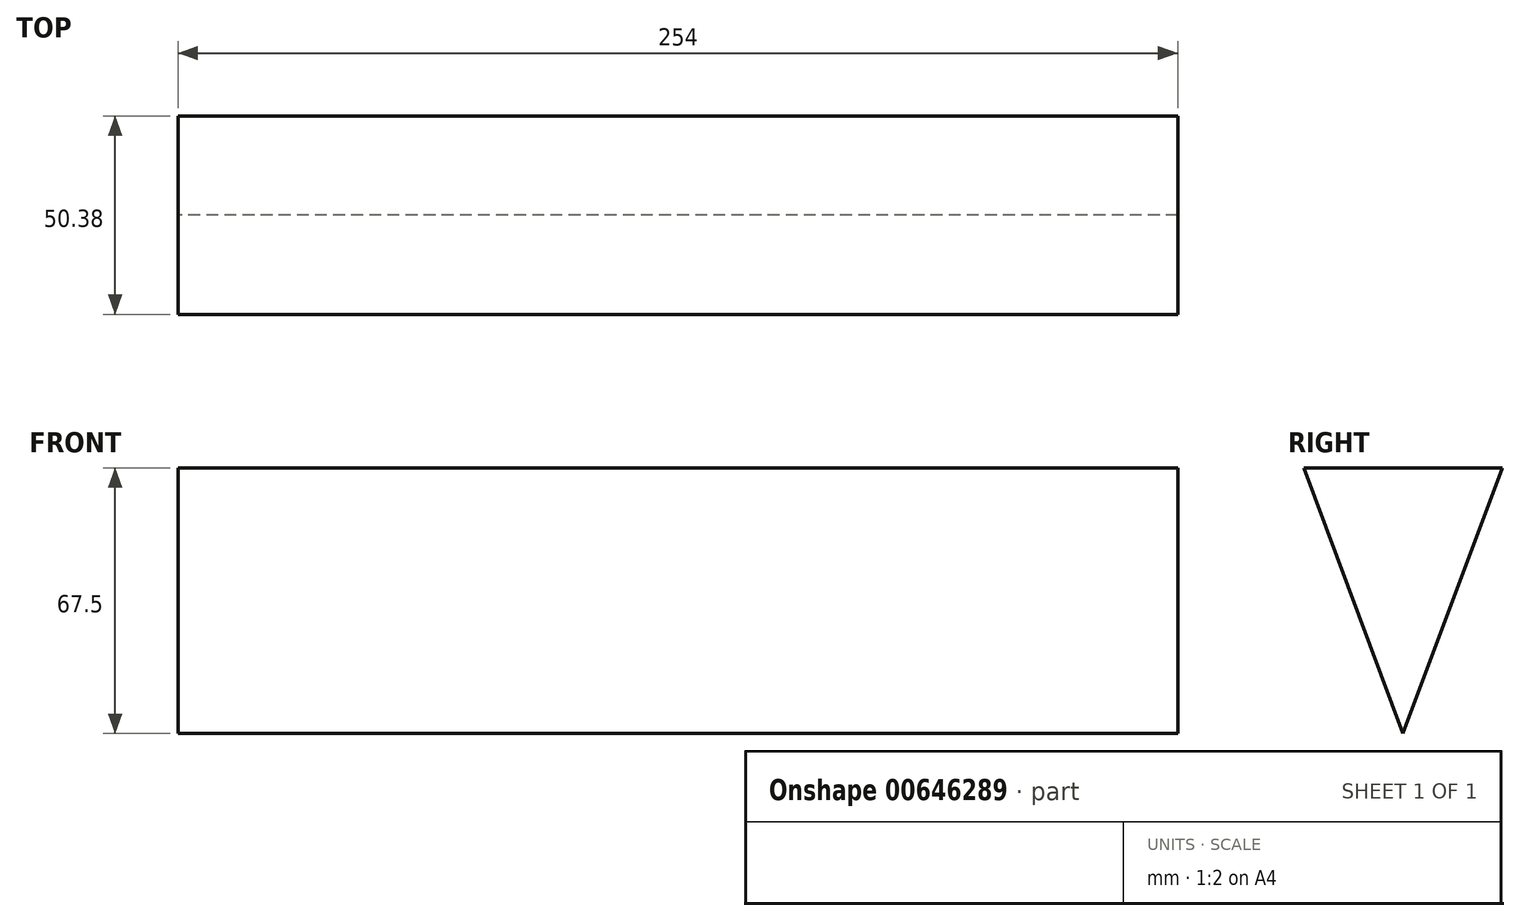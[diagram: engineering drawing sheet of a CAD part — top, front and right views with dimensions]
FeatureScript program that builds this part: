
annotation { "Feature Type Name" : "Feature", "Feature Type Description" : "" }
export const myFeature = defineFeature(function(context is Context, id is Id, definition is map)
    precondition{}
    {
        {
            var Q0;
            Q0=qCreatedBy(makeId("Right.planeOp"),FACE);
            var sketch = newSketch(context, id + "F0", { "sketchPlane" : qUnion([Q0])});
            skLineSegment(sketch, "E0", {"start": v(-20.12, 45) * mm, "end": v(30.26, 45) * mm});
            skLineSegment(sketch, "E1", {"start": v(5.07, -22.5) * mm, "end": v(30.26, 45) * mm});
            skLineSegment(sketch, "E2", {"start": v(5.07, -22.5) * mm, "end": v(-20.12, 45) * mm});
            skSolve(sketch);
        }
        {
            var Q0;
            Q0=makeQuery(id+"F0.imprint","IMPRINT",FACE,{"disambiguationData":[TD([[makeQuery(id+"F0.imprint","IMPRINT",EDGE,{"derivedFrom":sQuery(id+"F0.wireOp",EDGE,"E0")}),-1.0]])]});
            extrude(context, id + "F1", {"entities" : qUnion([Q0]), "depth" : 254 * mm, "offsetDistance" : 25.4 * mm});
        }
    });
